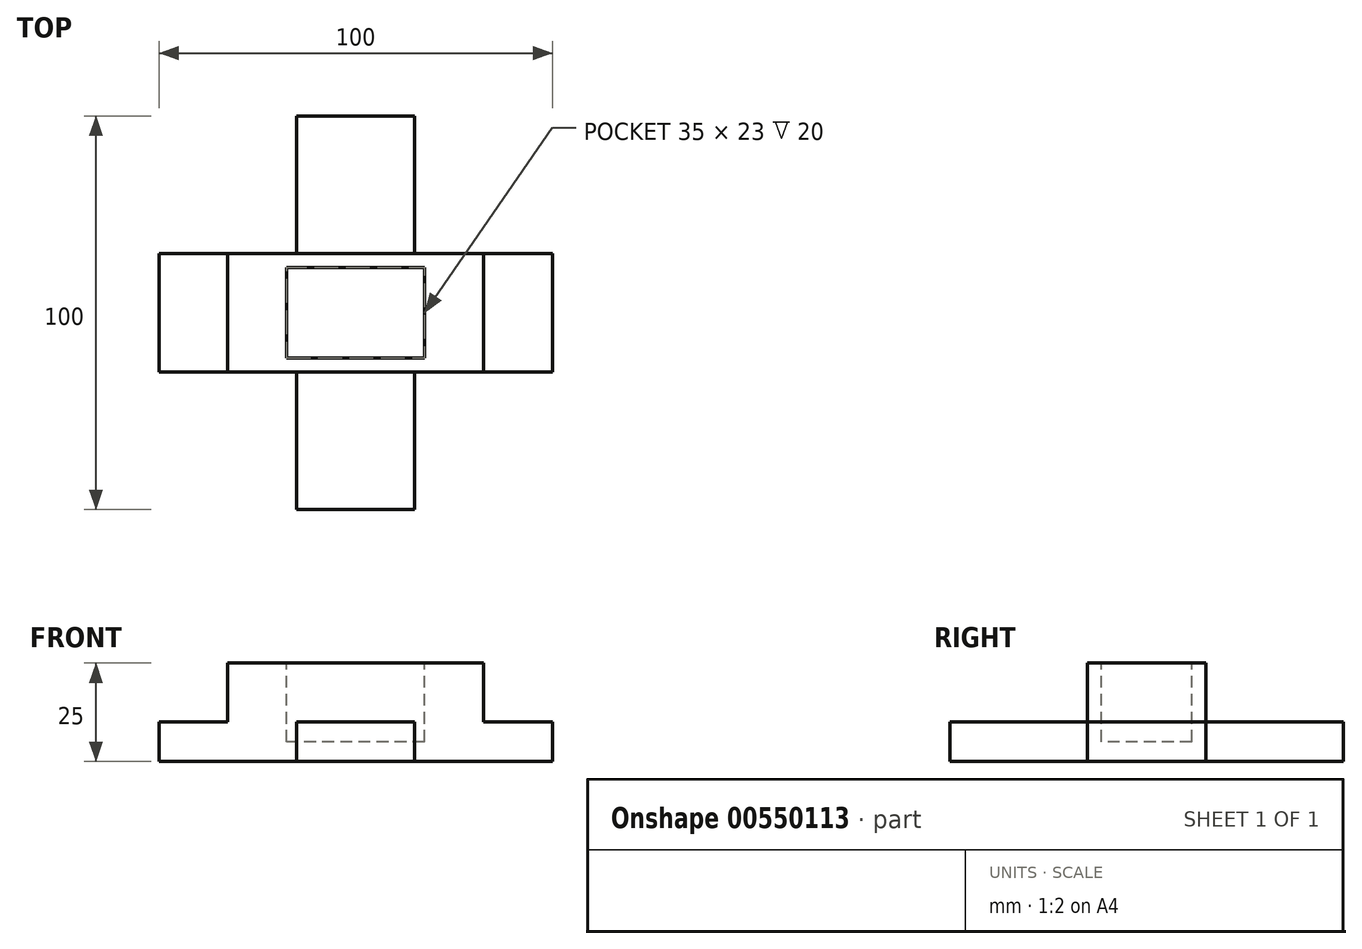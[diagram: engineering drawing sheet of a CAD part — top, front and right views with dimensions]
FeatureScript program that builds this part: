
annotation { "Feature Type Name" : "Feature", "Feature Type Description" : "" }
export const myFeature = defineFeature(function(context is Context, id is Id, definition is map)
    precondition{}
    {
        {
            var Q0;
            Q0=qCreatedBy(makeId("Top.planeOp"),FACE);
            var sketch = newSketch(context, id + "F0", { "sketchPlane" : qUnion([Q0])});
            skLineSegment(sketch, "E0.bottom", {"start": v(50, 50) * mm, "end": v(-50, 50) * mm});
            skLineSegment(sketch, "E0.top", {"start": v(50, -50) * mm, "end": v(-50, -50) * mm});
            skLineSegment(sketch, "E0.left", {"start": v(50, 50) * mm, "end": v(50, -50) * mm});
            skLineSegment(sketch, "E0.right", {"start": v(-50, 50) * mm, "end": v(-50, -50) * mm});
            skPoint(sketch, "E0.middle", {"position": v(0, 0) * mm});
            skLineSegment(sketch, "E1.bottom", {"start": v(-50, 50) * mm, "end": v(-15, 50) * mm});
            skLineSegment(sketch, "E1.top", {"start": v(-50, 15) * mm, "end": v(-15, 15) * mm});
            skLineSegment(sketch, "E1.left", {"start": v(-50, 50) * mm, "end": v(-50, 15) * mm});
            skLineSegment(sketch, "E1.right", {"start": v(-15, 50) * mm, "end": v(-15, 15) * mm});
            skLineSegment(sketch, "E2.MirrorCS", {"start": v(15, 50) * mm, "end": v(15, 15) * mm});
            skLineSegment(sketch, "E3.MirrorCS", {"start": v(50, 15) * mm, "end": v(15, 15) * mm});
            skLineSegment(sketch, "E4.MirrorCS", {"start": v(-50, -15) * mm, "end": v(-15, -15) * mm});
            skLineSegment(sketch, "E5.MirrorCS", {"start": v(-15, -50) * mm, "end": v(-15, -15) * mm});
            skLineSegment(sketch, "E6.MirrorCS", {"start": v(15, -50) * mm, "end": v(15, -15) * mm});
            skLineSegment(sketch, "E7.MirrorCS", {"start": v(50, -15) * mm, "end": v(15, -15) * mm});
            skSolve(sketch);
        }
        {
            var Q0;
            {var subQ3=sQuery(id+"F0.wireOp",EDGE,"E1.top");Q0=makeQuery(id+"F0.imprint","IMPRINT",FACE,{"disambiguationData":[TD([[makeQuery(id+"F0.imprint","IMPRINT",EDGE,{"derivedFrom":subQ3}),-1.0]])]});}
            extrude(context, id + "F1", {"entities" : qUnion([Q0]), "depth" : 10 * mm, "offsetDistance" : 25 * mm});
        }
        {
            var Q0;
            Q0=makeQuery(id+"F1.opExtrude","CAP_FACE",FACE,{"disambiguationData":[OSD([sQuery(id+"F0.wireOp",EDGE,"E0.bottom"),sQuery(id+"F0.wireOp",EDGE,"E0.top"),sQuery(id+"F0.wireOp",EDGE,"E0.left"),sQuery(id+"F0.wireOp",EDGE,"E0.right"),sQuery(id+"F0.wireOp",EDGE,"E1.top"),sQuery(id+"F0.wireOp",EDGE,"E1.right"),sQuery(id+"F0.wireOp",EDGE,"E2.MirrorCS"),sQuery(id+"F0.wireOp",EDGE,"E3.MirrorCS"),sQuery(id+"F0.wireOp",EDGE,"E4.MirrorCS"),sQuery(id+"F0.wireOp",EDGE,"E5.MirrorCS"),sQuery(id+"F0.wireOp",EDGE,"E6.MirrorCS"),sQuery(id+"F0.wireOp",EDGE,"E7.MirrorCS")])],"isStart":false});
            var sketch = newSketch(context, id + "F2", { "sketchPlane" : qUnion([Q0])});
            skLineSegment(sketch, "E8.bottom", {"start": v(15, 15) * mm, "end": v(-15, 15) * mm});
            skLineSegment(sketch, "E8.top", {"start": v(15, -15) * mm, "end": v(-15, -15) * mm});
            skPoint(sketch, "E8.middle", {"position": v(0, 0) * mm});
            skLineSegment(sketch, "E9", {"start": v(-32.5, 15) * mm, "end": v(-32.5, -15) * mm});
            skLineSegment(sketch, "E10", {"start": v(32.5, -15) * mm, "end": v(32.5, 15) * mm});
            skSolve(sketch);
        }
        {
            var Q0;
            {var subQ1=sQuery(id+"F2.wireOp",EDGE,"E8.bottom");Q0=makeQuery(id+"F2.imprint","IMPRINT",FACE,{"disambiguationData":[TD([[makeQuery(id+"F2.imprint","IMPRINT",EDGE,{"derivedFrom":subQ1}),1.0]])]});}
            extrude(context, id + "F3", {"entities" : qUnion([Q0]), "operationType" : NewBodyOperationType.ADD, "depth" : 15 * mm, "offsetDistance" : 25 * mm});
        }
        {
            var Q0;
            Q0=makeQuery(id+"F3.opExtrude","CAP_FACE",FACE,{"disambiguationData":[OSD([sQuery(id+"F0.wireOp",EDGE,"E1.top"),sQuery(id+"F0.wireOp",EDGE,"E3.MirrorCS"),sQuery(id+"F0.wireOp",EDGE,"E4.MirrorCS"),sQuery(id+"F0.wireOp",EDGE,"E7.MirrorCS"),sQuery(id+"F2.wireOp",EDGE,"E8.bottom"),sQuery(id+"F2.wireOp",EDGE,"E8.top"),sQuery(id+"F2.wireOp",EDGE,"E9"),sQuery(id+"F2.wireOp",EDGE,"E10")])],"isStart":false});
            var sketch = newSketch(context, id + "F4", { "sketchPlane" : qUnion([Q0])});
            skLineSegment(sketch, "E11.bottom", {"start": v(17.5, 11.5) * mm, "end": v(-17.5, 11.5) * mm});
            skLineSegment(sketch, "E11.top", {"start": v(17.5, -11.5) * mm, "end": v(-17.5, -11.5) * mm});
            skLineSegment(sketch, "E11.left", {"start": v(17.5, 11.5) * mm, "end": v(17.5, -11.5) * mm});
            skLineSegment(sketch, "E11.right", {"start": v(-17.5, 11.5) * mm, "end": v(-17.5, -11.5) * mm});
            skPoint(sketch, "E11.middle", {"position": v(0, 0) * mm});
            skSolve(sketch);
        }
        {
            var Q0;
            Q0 = qSketchRegion(id + "F4", true);
            extrude(context, id + "F5", {"entities" : qUnion([Q0]), "operationType" : NewBodyOperationType.REMOVE, "oppositeDirection" : true, "depth" : 20 * mm, "offsetDistance" : 25 * mm});
        }
    });
